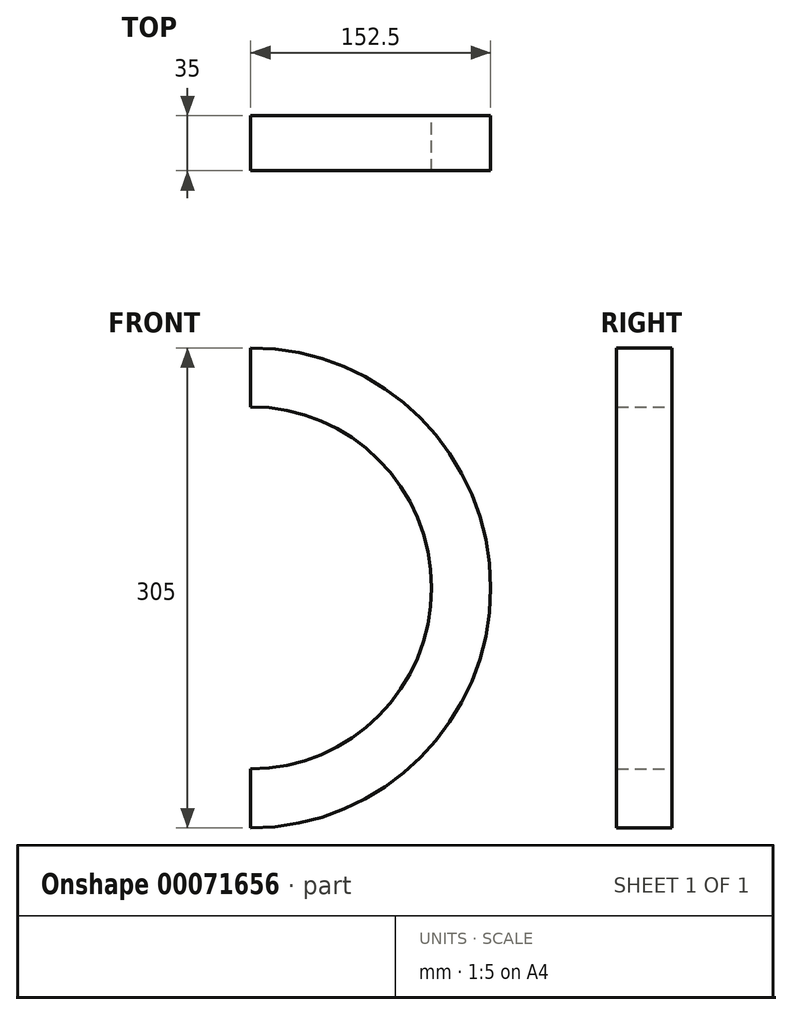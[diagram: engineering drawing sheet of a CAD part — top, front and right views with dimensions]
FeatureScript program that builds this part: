
annotation { "Feature Type Name" : "Feature", "Feature Type Description" : "" }
export const myFeature = defineFeature(function(context is Context, id is Id, definition is map)
    precondition{}
    {
        {
            var Q0;
            Q0=qCreatedBy(makeId("Front.planeOp"),FACE);
            var sketch = newSketch(context, id + "F0", { "sketchPlane" : qUnion([Q0])});
            skArc(sketch, "E0", {"start": v(0, -152.5) * mm, "mid": v(152.5, 0) * mm, "end": v(0, 152.5) * mm});
            skArc(sketch, "E1", {"start": v(0, -115) * mm, "mid": v(115, 0) * mm, "end": v(0, 115) * mm});
            skLineSegment(sketch, "E2", {"start": v(0, 115) * mm, "end": v(0, 152.5) * mm});
            skLineSegment(sketch, "E3", {"start": v(0, -115) * mm, "end": v(0, -152.5) * mm});
            skSolve(sketch);
        }
        {
            var Q0;
            Q0 = qSketchRegion(id + "F0", true);
            extrude(context, id + "F1", {"entities" : qUnion([Q0]), "depth" : 35 * mm});
        }
    });
